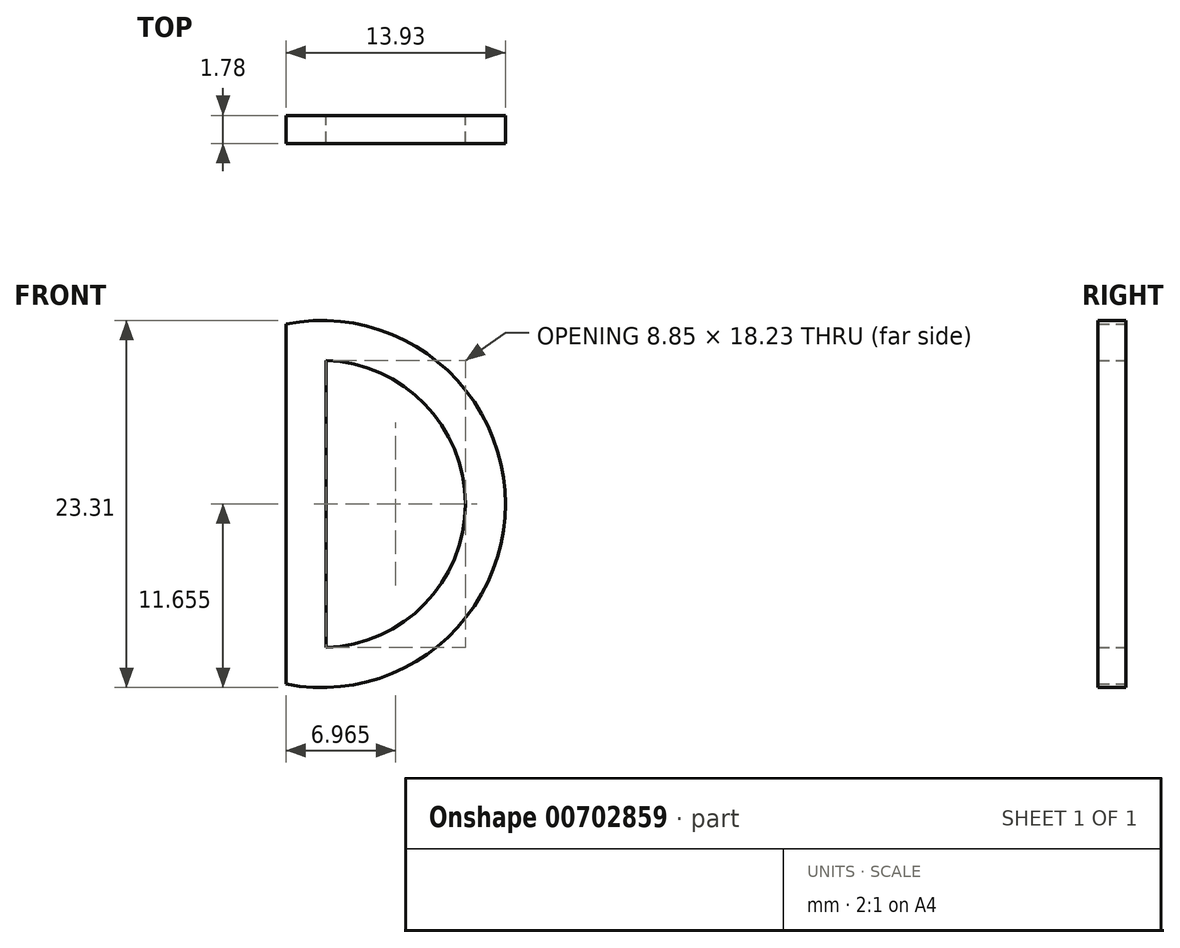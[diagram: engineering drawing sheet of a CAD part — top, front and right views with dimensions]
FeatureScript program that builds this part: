
annotation { "Feature Type Name" : "Feature", "Feature Type Description" : "" }
export const myFeature = defineFeature(function(context is Context, id is Id, definition is map)
    precondition{}
    {
        {
            var Q0;
            Q0=qCreatedBy(makeId("Front.planeOp"),FACE);
            var sketch = newSketch(context, id + "F0", { "sketchPlane" : qUnion([Q0])});
            skLineSegment(sketch, "E0", {"start": v(0, 8.81) * mm, "end": v(0, -14.06) * mm});
            skArc(sketch, "E1", {"start": v(0, -14.06) * mm, "mid": v(13.93, -2.62) * mm, "end": v(0, 8.81) * mm});
            skSolve(sketch);
        }
        {
            var Q0;
            Q0 = qSketchRegion(id + "F0", true);
            var Q1;
            Q1=makeQuery(id+"F0.imprint","IMPRINT",FACE,{"disambiguationData":[TD([[makeQuery(id+"F0.imprint","IMPRINT",EDGE,{"derivedFrom":sQuery(id+"F0.wireOp",EDGE,"E0")}),1.0]])]});
            extrude(context, id + "F1", {"entities" : qUnion([Q0, Q1]), "depth" : 1.78 * mm, "offsetDistance" : 25.4 * mm});
        }
        {
            var Q0;
            Q0=makeQuery(id+"F1.opExtrude","CAP_FACE",FACE,{"disambiguationData":[OSD([sQuery(id+"F0.wireOp",EDGE,"E0"),sQuery(id+"F0.wireOp",EDGE,"E1")])],"isStart":false});
            var Q1;
            Q1=makeQuery(id+"F1.opExtrude","CAP_FACE",FACE,{"disambiguationData":[OSD([sQuery(id+"F0.wireOp",EDGE,"E0"),sQuery(id+"F0.wireOp",EDGE,"E1")])],"isStart":true});
            shell(context, id + "F2", {"entities" : qUnion([Q0, Q1]), "thickness" : 2.54 * mm});
        }
    });
